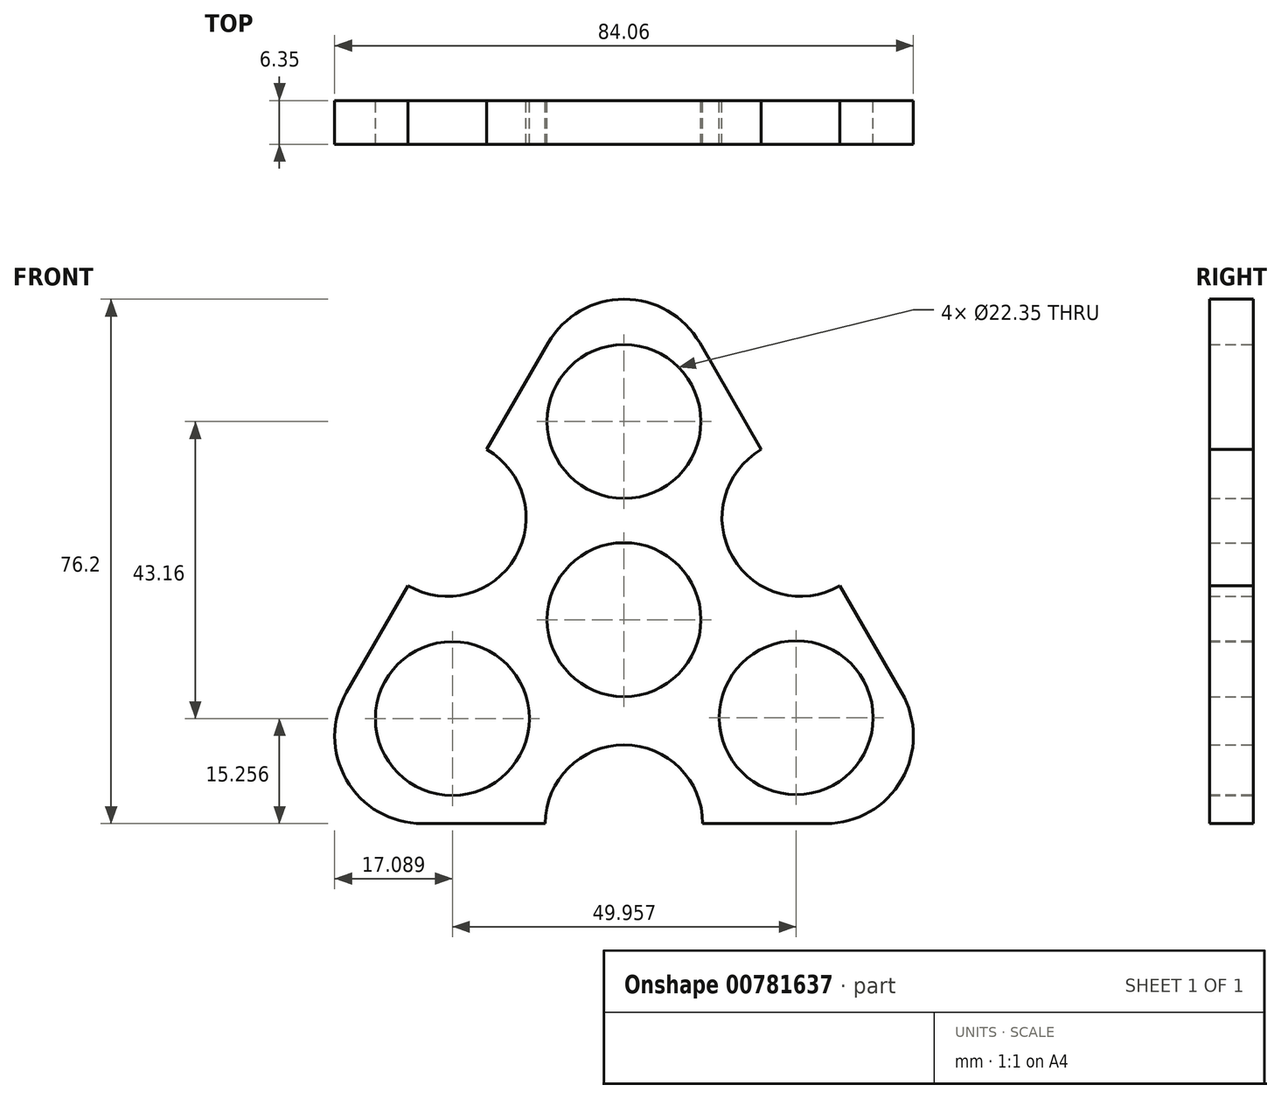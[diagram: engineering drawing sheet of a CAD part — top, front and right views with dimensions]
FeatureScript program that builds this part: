
annotation { "Feature Type Name" : "Feature", "Feature Type Description" : "" }
export const myFeature = defineFeature(function(context is Context, id is Id, definition is map)
    precondition{}
    {
        {
            var Q0;
            Q0=qCreatedBy(makeId("Front.planeOp"),FACE);
            var sketch = newSketch(context, id + "F0", { "sketchPlane" : qUnion([Q0])});
            skCircle(sketch, "E0.cCircle", {"center": v(0, 0) * mm, "radius": 29.63 * mm, "construction": true});
            skLineSegment(sketch, "E0.0", {"start": v(0, 59.27) * mm, "end": v(51.33, -29.63) * mm});
            skLineSegment(sketch, "E0.1", {"start": v(51.33, -29.63) * mm, "end": v(-51.33, -29.63) * mm});
            skLineSegment(sketch, "E0.2", {"start": v(-51.33, -29.63) * mm, "end": v(0, 59.27) * mm});
            skPoint(sketch, "E0.0.midPoint", {"position": v(25.66, 14.82) * mm});
            skCircle(sketch, "E1", {"center": v(-25.66, 14.82) * mm, "radius": 11.43 * mm});
            skCircle(sketch, "E2", {"center": v(0, -29.63) * mm, "radius": 11.43 * mm});
            skPoint(sketch, "E2.centerSnap0", {"position": v(0, -29.63) * mm});
            skCircle(sketch, "E3", {"center": v(25.66, 14.82) * mm, "radius": 11.43 * mm});
            skSolve(sketch);
        }
        {
            var Q0;
            {var subQ1=sQuery(id+"F0.wireOp",EDGE,"E0.0");var subQ8=sQuery(id+"F0.wireOp",EDGE,"E0.2");var subQ11=makeQuery(id+"F0.imprint","INTERSECT",VERTEX,{"derivedFrom":[subQ1,subQ8]});Q0=makeQuery(id+"F0.imprint","IMPRINT",FACE,{"disambiguationData":[TD([[makeQuery(id+"F0.imprint","IMPRINT",EDGE,{"disambiguationData":[TD([[subQ11,-1.0]])],"derivedFrom":subQ1}),-1.0]])]});}
            extrude(context, id + "F1", {"entities" : qUnion([Q0]), "depth" : 6.35 * mm, "offsetDistance" : 25.4 * mm});
        }
        {
            var Q0;
            Q0=makeQuery(id+"F1.opExtrude","CAP_FACE",FACE,{"disambiguationData":[OSD([sQuery(id+"F0.wireOp",EDGE,"E0.0"),sQuery(id+"F0.wireOp",EDGE,"E0.1"),sQuery(id+"F0.wireOp",EDGE,"E0.2"),sQuery(id+"F0.wireOp",EDGE,"E1"),sQuery(id+"F0.wireOp",EDGE,"E2"),sQuery(id+"F0.wireOp",EDGE,"E3")])],"isStart":false});
            var sketch = newSketch(context, id + "F2", { "sketchPlane" : qUnion([Q0])});
            skCircle(sketch, "E4", {"center": v(0, 0) * mm, "radius": 12.7 * mm});
            skSolve(sketch);
        }
        {
            var Q0;
            Q0 = qSketchRegion(id + "F2", true);
            extrude(context, id + "F3", {"entities" : qUnion([Q0]), "operationType" : NewBodyOperationType.ADD, "depth" : 0 * mm, "offsetDistance" : 25.4 * mm, "hasSecondDirection" : true, "secondDirectionOppositeDirection" : true, "secondDirectionDepth" : 3.3 * mm});
        }
        {
            var Q0;
            Q0=makeQuery(id+"F1.opExtrude","CAP_FACE",FACE,{"disambiguationData":[OSD([sQuery(id+"F0.wireOp",EDGE,"E0.0"),sQuery(id+"F0.wireOp",EDGE,"E0.1"),sQuery(id+"F0.wireOp",EDGE,"E0.2"),sQuery(id+"F0.wireOp",EDGE,"E1"),sQuery(id+"F0.wireOp",EDGE,"E2"),sQuery(id+"F0.wireOp",EDGE,"E3")])],"isStart":true});
            var sketch = newSketch(context, id + "F4", { "sketchPlane" : qUnion([Q0])});
            skCircle(sketch, "E5", {"center": v(0, 28.79) * mm, "radius": 11.18 * mm});
            skCircle(sketch, "E6", {"center": v(-25.02, -14.25) * mm, "radius": 11.18 * mm});
            skCircle(sketch, "E7", {"center": v(24.94, -14.37) * mm, "radius": 11.18 * mm});
            skSolve(sketch);
        }
        {
            var Q0;
            Q0 = qSketchRegion(id + "F4", true);
            extrude(context, id + "F5", {"entities" : qUnion([Q0]), "operationType" : NewBodyOperationType.REMOVE, "oppositeDirection" : true, "depth" : 25.4 * mm, "offsetDistance" : 25.4 * mm});
        }
        {
            var Q0;
            Q0=makeQuery(id+"F1.opExtrude","SWEPT_EDGE",EDGE,{"disambiguationData":[OSD([sQuery(id+"F0.wireOp",EDGE,"E0.0"),sQuery(id+"F0.wireOp",EDGE,"E0.2")])]});
            var Q1;
            Q1=makeQuery(id+"F1.opExtrude","SWEPT_EDGE",EDGE,{"disambiguationData":[OSD([sQuery(id+"F0.wireOp",EDGE,"E0.0"),sQuery(id+"F0.wireOp",EDGE,"E0.1")])]});
            var Q2;
            Q2=makeQuery(id+"F1.opExtrude","SWEPT_EDGE",EDGE,{"disambiguationData":[OSD([sQuery(id+"F0.wireOp",EDGE,"E0.1"),sQuery(id+"F0.wireOp",EDGE,"E0.2")])]});
            fillet(context, id + "F6", {"entities" : qUnion([Q0, Q1, Q2]), "radius" : 12.7 * mm, "tangentPropagation" : true, "allowEdgeOverflow" : false});
        }
        {
            var Q0;
            Q0=makeQuery(id+"F1.opExtrude","CAP_FACE",FACE,{"disambiguationData":[OSD([sQuery(id+"F0.wireOp",EDGE,"E0.0"),sQuery(id+"F0.wireOp",EDGE,"E0.1"),sQuery(id+"F0.wireOp",EDGE,"E0.2"),sQuery(id+"F0.wireOp",EDGE,"E1"),sQuery(id+"F0.wireOp",EDGE,"E2"),sQuery(id+"F0.wireOp",EDGE,"E3")])],"isStart":true});
            var sketch = newSketch(context, id + "F7", { "sketchPlane" : qUnion([Q0])});
            skCircle(sketch, "E8", {"center": v(0, 0) * mm, "radius": 11.18 * mm});
            skSolve(sketch);
        }
        {
            var Q0;
            Q0 = qSketchRegion(id + "F7", true);
            extrude(context, id + "F8", {"entities" : qUnion([Q0]), "operationType" : NewBodyOperationType.REMOVE, "oppositeDirection" : true, "depth" : 25.4 * mm, "offsetDistance" : 25.4 * mm});
        }
    });
